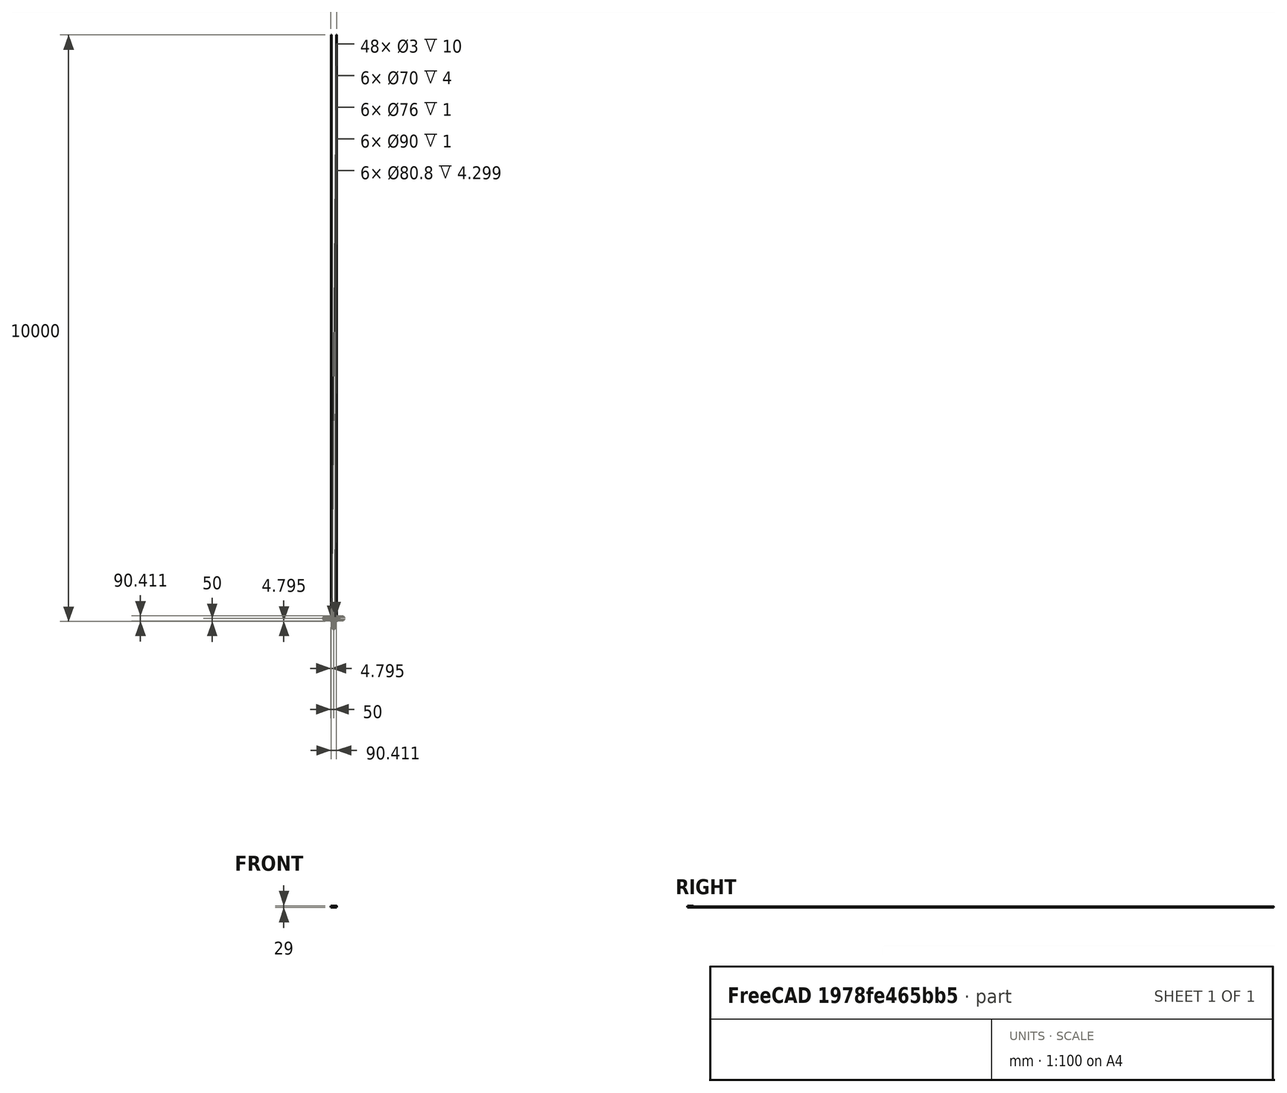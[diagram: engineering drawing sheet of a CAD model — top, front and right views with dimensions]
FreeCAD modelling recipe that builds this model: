
FCSTD DOCUMENT  (FreeCAD 0.16R6705 (Git))
Label: RingFixed
License: All rights reserved
LicenseURL: http://en.wikipedia.org/wiki/All_rights_reserved
objects: PartDesign::Fillet×16, Sketcher::SketchObject×14, PartDesign::Pocket×12, PartDesign::Chamfer×10, PartDesign::Pad×2, PartDesign::PolarPattern×2, PartDesign::Revolution×1, Part::Part2DObjectPython×1, Part::Cut×1, Part::Fuse×1
note: 75 computed .brp shape members not serialized (recipe doc carries the construction recipe); baked Part::Feature solids carry a one-line shape summary decoded from their .brp

FEATURE [Sketcher::SketchObject] Sketch013
  Placement = pos=(0,0,0) rot=(1,0,0;1.5708rad)
  sketch-geometry (25):
    g0: LineSegment StartX=14 StartY=0 StartZ=0 EndX=14 EndY=4 EndZ=0
    g1: LineSegment StartX=14 StartY=0 StartZ=0 EndX=45 EndY=0 EndZ=0
    g2: LineSegment StartX=14 StartY=4 StartZ=0 EndX=35 EndY=4 EndZ=0
    g3: LineSegment StartX=35 StartY=4 StartZ=0 EndX=35 EndY=20 EndZ=0
    g4: LineSegment StartX=45 StartY=0 StartZ=0 EndX=45 EndY=5.26261 EndZ=0
    g5: LineSegment StartX=35 StartY=20 StartZ=0 EndX=38 EndY=20 EndZ=0
    g6: LineSegment StartX=38 StartY=20 StartZ=0 EndX=38 EndY=21 EndZ=0
    g7: LineSegment StartX=38 StartY=21 StartZ=0 EndX=40.4 EndY=21 EndZ=0
    g8: LineSegment StartX=45 StartY=5.26261 StartZ=0 EndX=50 EndY=19 EndZ=0
    g9: LineSegment StartX=40.4 StartY=21 StartZ=0 EndX=40.4 EndY=25.2988 EndZ=0
    g10: LineSegment StartX=40.4 StartY=25.2988 StartZ=0 EndX=43.1012 EndY=28 EndZ=0
    g11: LineSegment StartX=45 StartY=29 StartZ=0 EndX=50 EndY=29 EndZ=0
    g12: LineSegment StartX=50 StartY=29 StartZ=0 EndX=50 EndY=19 EndZ=0
    g13: LineSegment StartX=43.1012 StartY=28 StartZ=0 EndX=45 EndY=28 EndZ=0
    g14: LineSegment StartX=45 StartY=28 StartZ=0 EndX=45 EndY=29 EndZ=0
    g15: Circle [constr] CenterX=40 CenterY=29 CenterZ=0 NormalX=0 NormalY=0 NormalZ=1 Radius=2.9
    g16: LineSegment [constr] StartX=40 StartY=29 StartZ=0 EndX=45 EndY=29 EndZ=0
    g17: Circle CenterX=44.1719 CenterY=24.8281 CenterZ=0 NormalX=0 NormalY=0 NormalZ=1 Radius=0.2
    g18: LineSegment [constr] StartX=42.0506 StartY=26.9494 StartZ=0 EndX=44.1719 EndY=24.8281 EndZ=0
    g19: Circle CenterX=39.5 CenterY=18 CenterZ=0 NormalX=0 NormalY=0 NormalZ=1 Radius=0.15
    g20: Circle CenterX=39.5 CenterY=16 CenterZ=0 NormalX=0 NormalY=0 NormalZ=1 Radius=0.15
    g21: Circle CenterX=39.5 CenterY=14 CenterZ=0 NormalX=0 NormalY=0 NormalZ=1 Radius=0.15
    g22: LineSegment [constr] StartX=39.5 StartY=21 StartZ=0 EndX=39.5 EndY=0 EndZ=0
    g23: Circle CenterX=39.5 CenterY=12 CenterZ=0 NormalX=0 NormalY=0 NormalZ=1 Radius=0.15
    g24: Circle CenterX=39.5 CenterY=10 CenterZ=0 NormalX=0 NormalY=0 NormalZ=1 Radius=0.15
  constraints (78):
    c: PointOnObject(g0,g-1)
    c: Vertical(g0)
    c: DistanceX(g-1,g0) = 14
    c: Coincident(g1,g0)
    c: Horizontal(g1)
    c: DistanceX(g-1,g1) = 45
    c: DistanceY(g0,g0) = -4
    c: Horizontal(g2)
    c: Coincident(g3,g2)
    c: Vertical(g3)
    c: Coincident(g2,g0)
    c: Coincident(g4,g1)
    c: Vertical(g4)
    c: Coincident(g5,g3)
    c: Horizontal(g5)
    c: Coincident(g6,g5)
    c: Vertical(g6)
    c: Coincident(g7,g6)
    c: Horizontal(g7)
    c: Coincident(g8,g4)
    c: Angle(g4,g8) = 2.79253
    c: DistanceX(g-1,g2) = 35
    c: DistanceY(g6,g2) = -17
    c: DistanceY(g5,g6) = 1
    c: DistanceX(g-1,g8) = 50
    c: DistanceX(g-1,g5) = 38
    c: Coincident(g7,g9)
    c: Vertical(g9)
    c: Coincident(g9,g10)
    c: Horizontal(g11)
    c: Coincident(g12,g11)
    c: Coincident(g12,g8)
    c: Vertical(g12)
    c: Coincident(g10,g13)
    c: Coincident(g13,g14)
    c: Coincident(g11,g14)
    c: Vertical(g14)
    c: Horizontal(g13)
    c: Radius(g15) = 2.9
    c: Tangent(g10,g15)
    c: Coincident(g16,g15)
    c: Horizontal(g16)
    c: Angle(g10,g16) = 2.35619
    c: DistanceX(g15,g9) = 0.4
    c: DistanceY(g10,g15) = 1
    c: Coincident(g11,g16)
    c: DistanceX(g-1,g13) = 45
    c: DistanceX(g-1,g15) = 40
    c: DistanceY(g6,g15) = 8
    c: DistanceY(g8,g11) = 10
    c: DistanceX(g11,g11) = 5
    c: DistanceX(g10,g13) = 1.89878
    c: DistanceY(g1,g11) = 29
    c: Radius(g17) = 0.2
    c: PointOnObject(g18,g15)
    c: PointOnObject(g18,g10)
    c: Angle(g10,g18) = 1.5708
    c: Coincident(g17,g18)
    c: Distance(g18,g17) = 3
    c: Vertical(g22)
    c: PointOnObject(g19,g22)
    c: PointOnObject(g20,g22)
    c: PointOnObject(g21,g22)
    c: Radius(g19) = 0.15
    c: Equal(g19,g20)
    c: Equal(g19,g21)
    c: PointOnObject(g22,g1)
    c: DistanceY(g19,g5) = 2
    c: DistanceY(g20,g19) = 2
    c: DistanceY(g21,g20) = 2
    c: PointOnObject(g22,g7)
    c: DistanceX(g5,g22) = 1.5
    c: PointOnObject(g23,g22)
    c: PointOnObject(g24,g22)
    c: Radius(g23) = 0.15
    c: Radius(g24) = 0.15
    c: DistanceY(g23,g21) = 2
    c: DistanceY(g24,g23) = 2
FEATURE [PartDesign::Revolution] Revolution
  Angle = 360
  Axis = (0,0,1)
  Base = (0,0,0)
  Placement = pos=(0,0,0) rot=(1,0,0;1.5708rad)
  ReferenceAxis = -> Sketch013 [V_Axis]
  Reversed = true
  Sketch = -> Sketch013
FEATURE [Part::Part2DObjectPython] InvoluteGear003  # Draft 2D object (typed FeaturePython)
  ExternalGear = true
  HighPrecision = true
  Modules = 1.5
  NumberOfTeeth = 18
  PressureAngle = 20
FEATURE [PartDesign::Pad] Pad007
  Length = 15
  Length2 = 10
  Placement = pos=(0,0,8) rot=(0,0,1;0rad)
  Sketch = -> InvoluteGear003
  Type = 0
FEATURE [Part::Cut] Cut
  Base = -> Revolution
  Tool = -> Pad007
FEATURE [Sketcher::SketchObject] Sketch014
  Placement = pos=(0,0,0) rot=(1,0,0;3.14159rad)
  Support = -> Cut [Face2]
  sketch-geometry (2):
    g0: Circle CenterX=0 CenterY=-20 CenterZ=0 NormalX=0 NormalY=0 NormalZ=1 Radius=1.7
    g1: Circle [constr] CenterX=0 CenterY=0 CenterZ=0 NormalX=0 NormalY=0 NormalZ=1 Radius=20
  constraints (5):
    c: Radius(g0) = 1.7
    c: Radius(g1) = 20
    c: Coincident(g1,g-1)
    c: PointOnObject(g0,g1)
    c: PointOnObject(g0,g-2)
FEATURE [PartDesign::Pocket] Pocket008
  Length = 5
  Sketch = -> Sketch014
  Type = 1
FEATURE [Sketcher::SketchObject] Sketch022  label="HorizontalMountPlane"
  sketch-geometry (48):
    g0: LineSegment StartX=-50 StartY=50 StartZ=0 EndX=50 EndY=50 EndZ=0
    g1: LineSegment StartX=50 StartY=50 StartZ=0 EndX=50 EndY=-50 EndZ=0
    g2: LineSegment StartX=50 StartY=-50 StartZ=0 EndX=-50 EndY=-50 EndZ=0
    g3: LineSegment StartX=-50 StartY=-50 StartZ=0 EndX=-50 EndY=50 EndZ=0
    g4: Circle CenterX=0 CenterY=0 CenterZ=0 NormalX=0 NormalY=0 NormalZ=1 Radius=44
    g5: LineSegment [constr] StartX=-44 StartY=44 StartZ=0 EndX=44 EndY=44 EndZ=0
    g6: LineSegment [constr] StartX=44 StartY=44 StartZ=0 EndX=44 EndY=-44 EndZ=0
    g7: LineSegment [constr] StartX=44 StartY=-44 StartZ=0 EndX=-44 EndY=-44 EndZ=0
    g8: LineSegment [constr] StartX=-44 StartY=-44 StartZ=0 EndX=-44 EndY=44 EndZ=0
    g9: LineSegment StartX=-47.25 StartY=47.25 StartZ=0 EndX=-40.75 EndY=47.25 EndZ=0
    g10: LineSegment StartX=-40.75 StartY=47.25 StartZ=0 EndX=-40.75 EndY=40.75 EndZ=0
    g11: LineSegment StartX=-40.75 StartY=40.75 StartZ=0 EndX=-47.25 EndY=40.75 EndZ=0
    g12: LineSegment StartX=-47.25 StartY=40.75 StartZ=0 EndX=-47.25 EndY=47.25 EndZ=0
    g13: LineSegment StartX=40.75 StartY=47.25 StartZ=0 EndX=47.25 EndY=47.25 EndZ=0
    g14: LineSegment StartX=47.25 StartY=47.25 StartZ=0 EndX=47.25 EndY=40.75 EndZ=0
    g15: LineSegment StartX=47.25 StartY=40.75 StartZ=0 EndX=40.75 EndY=40.75 EndZ=0
    g16: LineSegment StartX=40.75 StartY=40.75 StartZ=0 EndX=40.75 EndY=47.25 EndZ=0
    g17: LineSegment StartX=-47.25 StartY=-40.75 StartZ=0 EndX=-40.75 EndY=-40.75 EndZ=0
    g18: LineSegment StartX=-40.75 StartY=-40.75 StartZ=0 EndX=-40.75 EndY=-47.25 EndZ=0
    g19: LineSegment StartX=-40.75 StartY=-47.25 StartZ=0 EndX=-47.25 EndY=-47.25 EndZ=0
    g20: LineSegment StartX=-47.25 StartY=-47.25 StartZ=0 EndX=-47.25 EndY=-40.75 EndZ=0
    g21: LineSegment StartX=40.75 StartY=-40.75 StartZ=0 EndX=47.25 EndY=-40.75 EndZ=0
    g22: LineSegment StartX=47.25 StartY=-40.75 StartZ=0 EndX=47.25 EndY=-47.25 EndZ=0
    g23: LineSegment StartX=47.25 StartY=-47.25 StartZ=0 EndX=40.75 EndY=-47.25 EndZ=0
    g24: LineSegment StartX=40.75 StartY=-47.25 StartZ=0 EndX=40.75 EndY=-40.75 EndZ=0
    g25: LineSegment [constr] StartX=-47.25 StartY=40.75 StartZ=0 EndX=-47.25 EndY=-40.75 EndZ=0
    g26: LineSegment [constr] StartX=-40.75 StartY=47.25 StartZ=0 EndX=40.75 EndY=47.25 EndZ=0
    g27: LineSegment [constr] StartX=47.25 StartY=40.75 StartZ=0 EndX=47.25 EndY=-40.75 EndZ=0
    g28: Circle CenterX=-35 CenterY=44 CenterZ=0 NormalX=0 NormalY=0 NormalZ=1 Radius=1.7
    g29: Circle [constr] CenterX=-44 CenterY=35 CenterZ=0 NormalX=0 NormalY=0 NormalZ=1 Radius=1.7
    g30: Circle [constr] CenterX=-44 CenterY=-35 CenterZ=0 NormalX=0 NormalY=0 NormalZ=1 Radius=1.7
    g31: Circle CenterX=-35 CenterY=-44 CenterZ=0 NormalX=0 NormalY=0 NormalZ=1 Radius=1.7
    g32: Circle CenterX=35 CenterY=-44 CenterZ=0 NormalX=0 NormalY=0 NormalZ=1 Radius=1.7
    g33: Circle [constr] CenterX=44 CenterY=-35 CenterZ=0 NormalX=0 NormalY=0 NormalZ=1 Radius=1.7
    g34: Circle [constr] CenterX=44 CenterY=35 CenterZ=0 NormalX=0 NormalY=0 NormalZ=1 Radius=1.7
    g35: Circle CenterX=35 CenterY=44 CenterZ=0 NormalX=0 NormalY=0 NormalZ=1 Radius=1.7
    g36: LineSegment [constr] StartX=-44 StartY=35 StartZ=0 EndX=44 EndY=35 EndZ=0
    g37: LineSegment [constr] StartX=-35 StartY=44 StartZ=0 EndX=-35 EndY=-44 EndZ=0
    g38: LineSegment [constr] StartX=-44 StartY=-35 StartZ=0 EndX=44 EndY=-35 EndZ=0
    g39: LineSegment [constr] StartX=35 StartY=-44 StartZ=0 EndX=35 EndY=44 EndZ=0
    g40: LineSegment [constr] StartX=-36.5 StartY=36.5 StartZ=0 EndX=36.5 EndY=36.5 EndZ=0
    g41: LineSegment [constr] StartX=36.5 StartY=36.5 StartZ=0 EndX=36.5 EndY=-36.5 EndZ=0
    g42: LineSegment [constr] StartX=36.5 StartY=-36.5 StartZ=0 EndX=-36.5 EndY=-36.5 EndZ=0
    g43: LineSegment [constr] StartX=-36.5 StartY=-36.5 StartZ=0 EndX=-36.5 EndY=36.5 EndZ=0
    g44: Circle [constr] CenterX=-36.5 CenterY=36.5 CenterZ=0 NormalX=0 NormalY=0 NormalZ=1 Radius=1.7
    g45: Circle [constr] CenterX=36.5 CenterY=36.5 CenterZ=0 NormalX=0 NormalY=0 NormalZ=1 Radius=1.7
    g46: Circle [constr] CenterX=-36.5 CenterY=-36.5 CenterZ=0 NormalX=0 NormalY=0 NormalZ=1 Radius=1.7
    g47: Circle [constr] CenterX=36.5 CenterY=-36.5 CenterZ=0 NormalX=0 NormalY=0 NormalZ=1 Radius=1.7
  constraints (122):
    c: Coincident(g0,g1)
    c: Coincident(g1,g2)
    c: Coincident(g2,g3)
    c: Coincident(g3,g0)
    c: Horizontal(g0)
    c: Horizontal(g2)
    c: Vertical(g1)
    c: Vertical(g3)
    c: Symmetric(g2,g0,g-1)
    c: Coincident(g4,g-1)
    c: Radius(g4) = 44
    c: Equal(g0,g3)
    c: DistanceY(g2,g0) = 100
    c: Coincident(g5,g6)
    c: Coincident(g6,g7)
    c: Coincident(g7,g8)
    c: Coincident(g8,g5)
    c: Horizontal(g5)
    c: Horizontal(g7)
    c: Vertical(g6)
    c: Vertical(g8)
    c: Coincident(g9,g10)
    c: Coincident(g10,g11)
    c: Coincident(g11,g12)
    c: Coincident(g12,g9)
    c: Horizontal(g9)
    c: Horizontal(g11)
    c: Vertical(g10)
    c: Vertical(g12)
    c: Symmetric(g11,g9,g5)
    c: Equal(g12,g9)
    c: DistanceY(g11,g9) = 6.5
    c: Coincident(g13,g14)
    c: Coincident(g14,g15)
    c: Coincident(g15,g16)
    c: Coincident(g16,g13)
    c: Horizontal(g13)
    c: Horizontal(g15)
    c: Vertical(g14)
    c: Vertical(g16)
    c: Symmetric(g15,g13,g5)
    c: Equal(g14,g13)
    c: Coincident(g17,g18)
    c: Coincident(g18,g19)
    c: Coincident(g19,g20)
    c: Coincident(g20,g17)
    c: Horizontal(g17)
    c: Horizontal(g19)
    c: Vertical(g18)
    c: Vertical(g20)
    c: Coincident(g21,g22)
    c: Coincident(g22,g23)
    c: Coincident(g23,g24)
    c: Coincident(g24,g21)
    c: Horizontal(g21)
    c: Horizontal(g23)
    c: Vertical(g22)
    c: Vertical(g24)
    c: Symmetric(g21,g23,g6)
    c: Symmetric(g17,g18,g7)
    c: Equal(g17,g18)
    c: Equal(g21,g24)
    c: Coincident(g25,g11)
    c: Coincident(g25,g17)
    c: Vertical(g25)
    c: Coincident(g26,g9)
    c: Coincident(g26,g13)
    c: Horizontal(g26)
    c: Coincident(g27,g14)
    c: Coincident(g27,g21)
    c: Vertical(g27)
    c: Equal(g5,g8)
    c: DistanceY(g6,g5) = 88
    c: Symmetric(g10,g21,g-1)
    c: PointOnObject(g28,g5)
    c: PointOnObject(g29,g8)
    c: PointOnObject(g30,g8)
    c: PointOnObject(g31,g7)
    c: PointOnObject(g32,g7)
    c: PointOnObject(g33,g6)
    c: PointOnObject(g34,g6)
    c: PointOnObject(g35,g5)
    c: Radius(g30) = 1.7
    c: Equal(g30, g31-g35) x5
    c: Equal(g30,g28)
    c: Equal(g30,g29)
    c: DistanceY(g29,g5) = 9
    c: DistanceX(g5,g28) = 9
    c: Coincident(g36,g29)
    c: Coincident(g36,g34)
    c: Horizontal(g36)
    c: Coincident(g37,g28)
    c: Vertical(g37)
    c: Coincident(g31,g37)
    c: Coincident(g38,g30)
    c: Coincident(g38,g33)
    c: Horizontal(g38)
    c: Coincident(g39,g32)
    c: Coincident(g39,g35)
    c: Vertical(g39)
    c: Symmetric(g35,g28,g-2)
    c: Symmetric(g29,g30,g-1)
    c: Coincident(g40,g41)
    c: Coincident(g41,g42)
    c: Coincident(g42,g43)
    c: Coincident(g43,g40)
    c: Horizontal(g40)
    c: Horizontal(g42)
    c: Vertical(g41)
    c: Vertical(g43)
    c: Equal(g41,g40)
    c: Symmetric(g40,g42,g-1)
    c: Coincident(g44,g40)
    c: Coincident(g45,g40)
    c: Coincident(g47,g41)
    c: Radius(g44) = 1.7
    c: Equal(g44,g45)
    c: Equal(g44,g47)
    c: Equal(g44,g46)
    c: DistanceX(g40,g40) = 73
    c: Coincident(g46,g42)
    c: DistanceX(g31,g32) = 70
FEATURE [PartDesign::Pad] Pad012
  Length = 29
  Length2 = 100
  Sketch = -> Sketch022
  Type = 0
FEATURE [Sketcher::SketchObject] Sketch023
  Placement = pos=(0,0,29) rot=(0,0,1;0rad)
  Support = -> Pad012 [Face27]
  sketch-geometry (1):
    g0: Circle CenterX=0 CenterY=0 CenterZ=0 NormalX=0 NormalY=0 NormalZ=1 Radius=49
  constraints (2):
    c: Coincident(g0,g-1)
    c: Radius(g0) = 49
FEATURE [PartDesign::Pocket] Pocket014
  Length = 10
  Sketch = -> Sketch023
  Type = 0
FEATURE [PartDesign::PolarPattern] PolarPattern
  Angle = 360
  Axis = -> Sketch014 [N_Axis]
  Occurrences = 6
  Originals = -> [Pocket008]
FEATURE [Sketcher::SketchObject] Sketch  label="BearingScrewHoles"
  Placement = pos=(0,0,29) rot=(0,0,1;0rad)
  Support = -> PolarPattern [Face399]
  sketch-geometry (2):
    g0: Circle CenterX=45.2053 CenterY=12.1127 CenterZ=0 NormalX=0 NormalY=0 NormalZ=1 Radius=1.5
    g1: LineSegment [constr] StartX=0 StartY=0 StartZ=0 EndX=45.2053 EndY=12.1127 EndZ=0
  constraints (5):
    c: Radius(g0) = 1.5
    c: Coincident(g1,g-1)
    c: Coincident(g1,g0)
    c: Distance(g-1,g0) = 46.8
    c: Angle(g-1,g1) = 0.261799
FEATURE [PartDesign::Pocket] Pocket
  Length = 12
  Sketch = -> Sketch
  Type = 0
FEATURE [PartDesign::PolarPattern] PolarPattern001
  Angle = 360
  Axis = -> Sketch [N_Axis]
  Occurrences = 12
  Originals = -> [Pocket]
FEATURE [Part::Fuse] Fusion001
  Base = -> Pocket014
  Tool = -> PolarPattern001
FEATURE [Sketcher::SketchObject] Sketch024  label="VerticalMountPlane"
  Placement = pos=(0,-50,0) rot=(1,0,0;1.5708rad)
  Support = -> Fusion001 [Face4]
  sketch-geometry (13):
    g0: LineSegment StartX=-47.25 StartY=9.25 StartZ=0 EndX=-40.75 EndY=9.25 EndZ=0
    g1: LineSegment StartX=-40.75 StartY=9.25 StartZ=0 EndX=-40.75 EndY=2.75 EndZ=0
    g2: LineSegment StartX=-40.75 StartY=2.75 StartZ=0 EndX=-47.25 EndY=2.75 EndZ=0
    g3: LineSegment StartX=-47.25 StartY=2.75 StartZ=0 EndX=-47.25 EndY=9.25 EndZ=0
    g4: LineSegment StartX=40.75 StartY=9.25 StartZ=0 EndX=47.25 EndY=9.25 EndZ=0
    g5: LineSegment StartX=47.25 StartY=9.25 StartZ=0 EndX=47.25 EndY=2.75 EndZ=0
    g6: LineSegment StartX=47.25 StartY=2.75 StartZ=0 EndX=40.75 EndY=2.75 EndZ=0
    g7: LineSegment StartX=40.75 StartY=2.75 StartZ=0 EndX=40.75 EndY=9.25 EndZ=0
    g8: GeomPoint [constr] X=-44 Y=6 Z=0
    g9: GeomPoint [constr] X=44 Y=6 Z=0
    g10: Circle CenterX=-44 CenterY=16 CenterZ=0 NormalX=0 NormalY=0 NormalZ=1 Radius=0.15
    g11: Circle CenterX=44 CenterY=16 CenterZ=0 NormalX=0 NormalY=0 NormalZ=1 Radius=0.15
    g12: LineSegment [constr] StartX=-44 StartY=6 StartZ=0 EndX=-44 EndY=16 EndZ=0
  constraints (31):
    c: Coincident(g0,g1)
    c: Coincident(g1,g2)
    c: Coincident(g2,g3)
    c: Coincident(g3,g0)
    c: Horizontal(g0)
    c: Horizontal(g2)
    c: Vertical(g1)
    c: Vertical(g3)
    c: Coincident(g4,g5)
    c: Coincident(g5,g6)
    c: Coincident(g6,g7)
    c: Coincident(g7,g4)
    c: Horizontal(g4)
    c: Horizontal(g6)
    c: Vertical(g5)
    c: Vertical(g7)
    c: Symmetric(g1,g6,g-2)
    c: Symmetric(g0,g4,g-2)
    c: Equal(g1,g2)
    c: DistanceX(g2,g1) = 6.5
    c: Symmetric(g2,g0,g8)
    c: Symmetric(g4,g6,g9)
    c: DistanceX(g8,g9) = 88
    c: DistanceY(g-1,g8) = 6
    c: Coincident(g12,g8)
    c: Coincident(g12,g10)
    c: Vertical(g12)
    c: Radius(g10) = 0.15
    c: DistanceY(g8,g10) = 10
    c: Symmetric(g10,g11,g-2)
    c: Equal(g11,g10)
FEATURE [PartDesign::Pocket] Pocket015  label="MainBlock"
  Length = 5
  Sketch = -> Sketch024
  Type = 1
FEATURE [Sketcher::SketchObject] Sketch025  label="SideScrewHoles"
  Placement = pos=(0,50,0) rot=(0,0.707107,0.707107;3.14159rad)
  Support = -> Pocket015 [Face1]
  sketch-geometry (5):
    g0: Circle CenterX=30 CenterY=21 CenterZ=0 NormalX=0 NormalY=0 NormalZ=1 Radius=1.4
    g1: Circle CenterX=-30 CenterY=21 CenterZ=0 NormalX=0 NormalY=0 NormalZ=1 Radius=1.4
    g2: LineSegment [constr] StartX=-30 StartY=21 StartZ=0 EndX=30 EndY=21 EndZ=0
    g3: Circle CenterX=-20 CenterY=21 CenterZ=0 NormalX=0 NormalY=0 NormalZ=1 Radius=1.4
    g4: Circle CenterX=20 CenterY=21 CenterZ=0 NormalX=0 NormalY=0 NormalZ=1 Radius=1.4
  constraints (13):
    c: Coincident(g2,g1)
    c: Coincident(g2,g0)
    c: Radius(g0) = 1.4
    c: Equal(g0,g1)
    c: DistanceX(g1,g0) = 60
    c: DistanceY(g-1,g1) = 21
    c: PointOnObject(g3,g2)
    c: Radius(g3) = 1.4
    c: PointOnObject(g4,g2)
    c: Radius(g4) = 1.4
    c: Symmetric(g1,g0,g-2)
    c: Symmetric(g3,g4,g-2)
    c: DistanceX(g3,g4) = 40
FEATURE [PartDesign::Pocket] Pocket016
  Length = 11
  Sketch = -> Sketch025
  Type = 0
FEATURE [Sketcher::SketchObject] Sketch026
  Placement = pos=(0,-50,0) rot=(1,0,0;1.5708rad)
  Support = -> Pocket016 [Face20]
  sketch-geometry (4):
    g0: LineSegment StartX=-30 StartY=9 StartZ=0 EndX=30 EndY=9 EndZ=0
    g1: LineSegment StartX=30 StartY=9 StartZ=0 EndX=30 EndY=0 EndZ=0
    g2: LineSegment StartX=30 StartY=0 StartZ=0 EndX=-30 EndY=0 EndZ=0
    g3: LineSegment StartX=-30 StartY=0 StartZ=0 EndX=-30 EndY=9 EndZ=0
  constraints (12):
    c: Coincident(g0,g1)
    c: Coincident(g1,g2)
    c: Coincident(g2,g3)
    c: Coincident(g3,g0)
    c: Horizontal(g0)
    c: Horizontal(g2)
    c: Vertical(g1)
    c: Vertical(g3)
    c: Symmetric(g1,g2,g-2)
    c: DistanceY(g-1,g2) = 0
    c: DistanceY(g2,g0) = 9
    c: DistanceX(g0,g0) = 60
FEATURE [PartDesign::Pocket] Pocket017
  Length = 8
  Sketch = -> Sketch026
  Type = 0
FEATURE [Sketcher::SketchObject] Sketch027  label="SideScrewHoles001"
  Placement = pos=(0,-50,0) rot=(1,0,0;1.5708rad)
  Support = -> Pocket017 [Face20]
  sketch-geometry (5):
    g0: Circle CenterX=30 CenterY=21 CenterZ=0 NormalX=0 NormalY=0 NormalZ=1 Radius=1.4
    g1: Circle CenterX=-30 CenterY=21 CenterZ=0 NormalX=0 NormalY=0 NormalZ=1 Radius=1.4
    g2: LineSegment [constr] StartX=-30 StartY=21 StartZ=0 EndX=30 EndY=21 EndZ=0
    g3: Circle CenterX=-20 CenterY=21 CenterZ=0 NormalX=0 NormalY=0 NormalZ=1 Radius=1.4
    g4: Circle CenterX=20 CenterY=21 CenterZ=0 NormalX=0 NormalY=0 NormalZ=1 Radius=1.4
  constraints (13):
    c: Coincident(g2,g1)
    c: Coincident(g2,g0)
    c: Radius(g0) = 1.4
    c: Equal(g0,g1)
    c: DistanceX(g1,g0) = 60
    c: DistanceY(g-1,g1) = 21
    c: PointOnObject(g3,g2)
    c: Radius(g3) = 1.4
    c: PointOnObject(g4,g2)
    c: Radius(g4) = 1.4
    c: Symmetric(g1,g0,g-2)
    c: Symmetric(g3,g4,g-2)
    c: DistanceX(g3,g4) = 40
FEATURE [PartDesign::Pocket] Pocket018
  Length = 11
  Sketch = -> Sketch027
  Type = 0
FEATURE [Sketcher::SketchObject] Sketch028  label="Recess001"
  Placement = pos=(0,50,0) rot=(0,0.707107,0.707107;3.14159rad)
  Support = -> Pocket018 [Face1]
  sketch-geometry (4):
    g0: LineSegment StartX=-30 StartY=9 StartZ=0 EndX=30 EndY=9 EndZ=0
    g1: LineSegment StartX=30 StartY=9 StartZ=0 EndX=30 EndY=0 EndZ=0
    g2: LineSegment StartX=30 StartY=0 StartZ=0 EndX=-30 EndY=0 EndZ=0
    g3: LineSegment StartX=-30 StartY=0 StartZ=0 EndX=-30 EndY=9 EndZ=0
  constraints (12):
    c: Coincident(g0,g1)
    c: Coincident(g1,g2)
    c: Coincident(g2,g3)
    c: Coincident(g3,g0)
    c: Horizontal(g0)
    c: Horizontal(g2)
    c: Vertical(g1)
    c: Vertical(g3)
    c: Symmetric(g1,g2,g-2)
    c: DistanceY(g-1,g2) = 0
    c: DistanceY(g2,g0) = 9
    c: DistanceX(g0,g0) = 60
FEATURE [PartDesign::Pocket] Pocket019  label="AnotherBrickInTheWall"
  Length = 8
  Sketch = -> Sketch028
  Type = 0
FEATURE [Sketcher::SketchObject] Sketch029  label="SideScrewHoles002"
  Placement = pos=(50,0,0) rot=(0.57735,0.57735,0.57735;2.0944rad)
  Support = -> Pocket019 [Face6]
  sketch-geometry (5):
    g0: Circle CenterX=30 CenterY=21 CenterZ=0 NormalX=0 NormalY=0 NormalZ=1 Radius=1.4
    g1: Circle CenterX=-30 CenterY=21 CenterZ=0 NormalX=0 NormalY=0 NormalZ=1 Radius=1.4
    g2: LineSegment [constr] StartX=-30 StartY=21 StartZ=0 EndX=30 EndY=21 EndZ=0
    g3: Circle CenterX=-20 CenterY=21 CenterZ=0 NormalX=0 NormalY=0 NormalZ=1 Radius=1.4
    g4: Circle CenterX=20 CenterY=21 CenterZ=0 NormalX=0 NormalY=0 NormalZ=1 Radius=1.4
  constraints (13):
    c: Coincident(g2,g1)
    c: Coincident(g2,g0)
    c: Radius(g0) = 1.4
    c: Equal(g0,g1)
    c: DistanceX(g1,g0) = 60
    c: DistanceY(g-1,g1) = 21
    c: PointOnObject(g3,g2)
    c: Radius(g3) = 1.4
    c: PointOnObject(g4,g2)
    c: Radius(g4) = 1.4
    c: Symmetric(g1,g0,g-2)
    c: Symmetric(g3,g4,g-2)
    c: DistanceX(g3,g4) = 40
FEATURE [PartDesign::Pocket] Pocket020
  Length = 11
  Sketch = -> Sketch029
  Type = 0
FEATURE [Sketcher::SketchObject] Sketch030  label="SideScrewHoles003"
  Placement = pos=(-50,0,0) rot=(0.57735,-0.57735,-0.57735;2.0944rad)
  Support = -> Pocket020 [Face8]
  sketch-geometry (5):
    g0: Circle CenterX=30 CenterY=21 CenterZ=0 NormalX=0 NormalY=0 NormalZ=1 Radius=1.4
    g1: Circle CenterX=-30 CenterY=21 CenterZ=0 NormalX=0 NormalY=0 NormalZ=1 Radius=1.4
    g2: LineSegment [constr] StartX=-30 StartY=21 StartZ=0 EndX=30 EndY=21 EndZ=0
    g3: Circle CenterX=-20 CenterY=21 CenterZ=0 NormalX=0 NormalY=0 NormalZ=1 Radius=1.4
    g4: Circle CenterX=20 CenterY=21 CenterZ=0 NormalX=0 NormalY=0 NormalZ=1 Radius=1.4
  constraints (13):
    c: Coincident(g2,g1)
    c: Coincident(g2,g0)
    c: Radius(g0) = 1.4
    c: Equal(g0,g1)
    c: DistanceX(g1,g0) = 60
    c: DistanceY(g-1,g1) = 21
    c: PointOnObject(g3,g2)
    c: Radius(g3) = 1.4
    c: PointOnObject(g4,g2)
    c: Radius(g4) = 1.4
    c: Symmetric(g1,g0,g-2)
    c: Symmetric(g3,g4,g-2)
    c: DistanceX(g3,g4) = 40
FEATURE [PartDesign::Pocket] Pocket021  label="FinalBeforeChamfer"
  Length = 11
  Sketch = -> Sketch030
  Type = 0
FEATURE [PartDesign::Chamfer] Chamfer
  Base = -> Pocket021 [Edge3]
  Size = 7.9
FEATURE [PartDesign::Chamfer] Chamfer001
  Base = -> Chamfer [Edge200]
  Size = 7.9
FEATURE [Sketcher::SketchObject] Sketch031  label="Recess"
  Placement = pos=(50,0,0) rot=(0.57735,0.57735,0.57735;2.0944rad)
  Support = -> Chamfer001 [Face8]
  sketch-geometry (4):
    g0: LineSegment StartX=-30 StartY=9.6 StartZ=0 EndX=30 EndY=9.6 EndZ=0
    g1: LineSegment StartX=30 StartY=9.6 StartZ=0 EndX=30 EndY=0 EndZ=0
    g2: LineSegment StartX=30 StartY=0 StartZ=0 EndX=-30 EndY=0 EndZ=0
    g3: LineSegment StartX=-30 StartY=0 StartZ=0 EndX=-30 EndY=9.6 EndZ=0
  constraints (12):
    c: Coincident(g0,g1)
    c: Coincident(g1,g2)
    c: Coincident(g2,g3)
    c: Coincident(g3,g0)
    c: Horizontal(g0)
    c: Horizontal(g2)
    c: Vertical(g1)
    c: Vertical(g3)
    c: Symmetric(g1,g2,g-2)
    c: DistanceY(g-1,g2) = 0
    c: DistanceY(g2,g0) = 9.6
    c: DistanceX(g0,g0) = 60
FEATURE [PartDesign::Pocket] Pocket022
  Length = 9.5
  Sketch = -> Sketch031
  Type = 0
FEATURE [PartDesign::Chamfer] Chamfer002
  Base = -> Pocket022 [Edge121]
  Size = 9.3
FEATURE [Sketcher::SketchObject] Sketch032
  Placement = pos=(-50,0,0) rot=(0.57735,-0.57735,-0.57735;2.0944rad)
  Support = -> Chamfer002 [Face25]
  sketch-geometry (4):
    g0: LineSegment StartX=-30 StartY=9.6 StartZ=0 EndX=30 EndY=9.6 EndZ=0
    g1: LineSegment StartX=30 StartY=9.6 StartZ=0 EndX=30 EndY=0 EndZ=0
    g2: LineSegment StartX=30 StartY=0 StartZ=0 EndX=-30 EndY=0 EndZ=0
    g3: LineSegment StartX=-30 StartY=0 StartZ=0 EndX=-30 EndY=9.6 EndZ=0
  constraints (12):
    c: Coincident(g0,g1)
    c: Coincident(g1,g2)
    c: Coincident(g2,g3)
    c: Coincident(g3,g0)
    c: Horizontal(g0)
    c: Horizontal(g2)
    c: Vertical(g1)
    c: Vertical(g3)
    c: Symmetric(g1,g2,g-2)
    c: DistanceY(g-1,g2) = 0
    c: DistanceY(g2,g0) = 9.6
    c: DistanceX(g0,g0) = 60
FEATURE [PartDesign::Pocket] Pocket023
  Length = 9.5
  Sketch = -> Sketch032
  Type = 0
FEATURE [PartDesign::Chamfer] Chamfer003
  Base = -> Pocket023 [Edge200]
  Size = 9.3
FEATURE [PartDesign::Fillet] Fillet
  Base = -> Chamfer003 [Edge6]
  Radius = 2
FEATURE [PartDesign::Fillet] Fillet001
  Base = -> Fillet [Edge151]
  Radius = 2
FEATURE [PartDesign::Fillet] Fillet002
  Base = -> Fillet001 [Edge84]
  Radius = 2
FEATURE [PartDesign::Fillet] Fillet003
  Base = -> Fillet002 [Edge79]
  Radius = 2
FEATURE [PartDesign::Fillet] Fillet004
  Base = -> Fillet003 [Edge56]
  Radius = 3
FEATURE [PartDesign::Fillet] Fillet005
  Base = -> Fillet004 [Edge85]
  Radius = 3
FEATURE [PartDesign::Fillet] Fillet006
  Base = -> Fillet005 [Edge64]
  Radius = 3
FEATURE [PartDesign::Fillet] Fillet007
  Base = -> Fillet006 [Edge66]
  Radius = 3
FEATURE [PartDesign::Fillet] Fillet008
  Base = -> Fillet007 [Edge156]
  Radius = 3
FEATURE [PartDesign::Fillet] Fillet009
  Base = -> Fillet008 [Edge89]
  Radius = 3
FEATURE [PartDesign::Fillet] Fillet010
  Base = -> Fillet009 [Edge77]
  Radius = 3
FEATURE [PartDesign::Fillet] Fillet011
  Base = -> Fillet010 [Edge63]
  Radius = 3
FEATURE [PartDesign::Fillet] Fillet012
  Base = -> Fillet011 [Edge109]
  Radius = 2
FEATURE [PartDesign::Fillet] Fillet013
  Base = -> Fillet012 [Edge70]
  Radius = 2
FEATURE [PartDesign::Fillet] Fillet014
  Base = -> Fillet013 [Edge192]
  Radius = 2
FEATURE [PartDesign::Fillet] Fillet015
  Base = -> Fillet014 [Edge72]
  Radius = 2
FEATURE [PartDesign::Chamfer] Chamfer004
  Base = -> Fillet015 [Edge329]
  Size = 1.5
FEATURE [PartDesign::Chamfer] Chamfer005
  Base = -> Chamfer004 [Edge71]
  Size = 1.5
FEATURE [PartDesign::Chamfer] Chamfer006
  Base = -> Chamfer005 [Edge5]
  Size = 1.5
FEATURE [PartDesign::Chamfer] Chamfer007
  Base = -> Chamfer006 [Edge6]
  Size = 1.5
FEATURE [PartDesign::Chamfer] Chamfer008
  Base = -> Chamfer007 [Edge7]
  Size = 1.5
FEATURE [PartDesign::Chamfer] Chamfer009
  Base = -> Chamfer008 [Edge8]
  Size = 1.5
